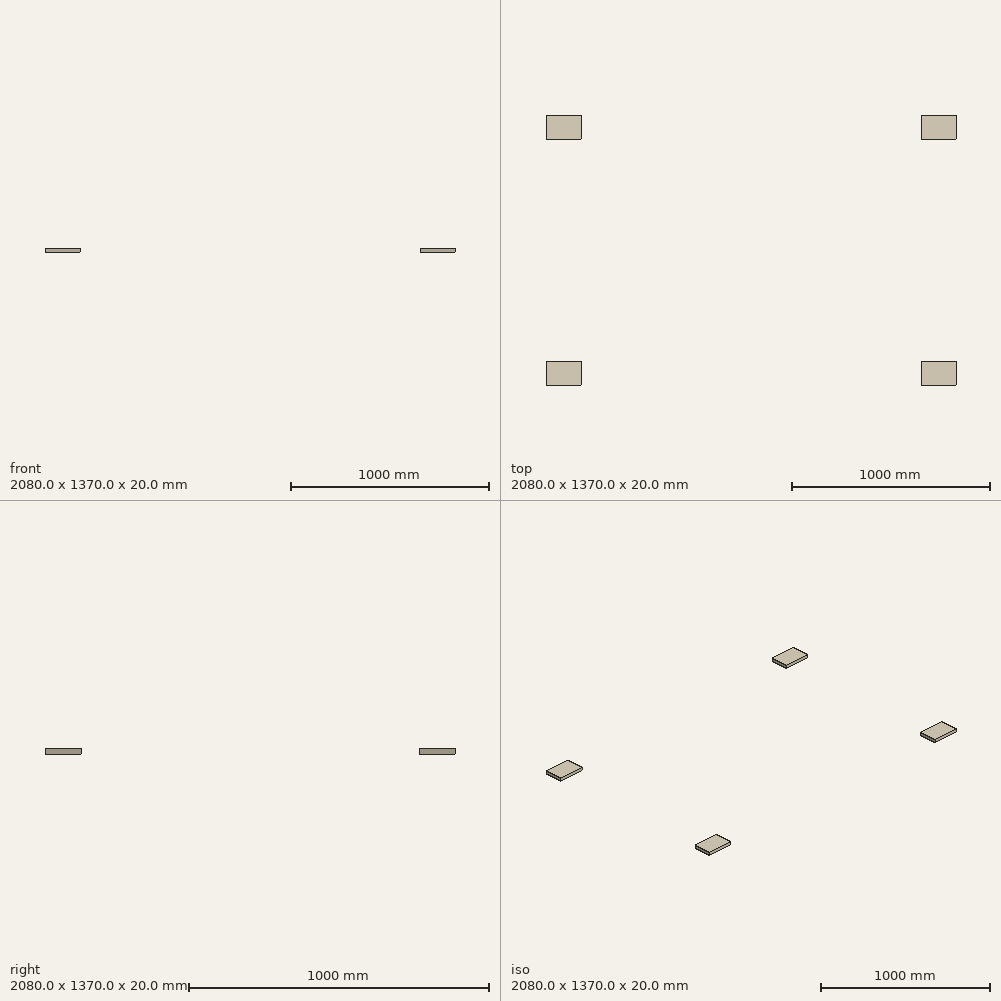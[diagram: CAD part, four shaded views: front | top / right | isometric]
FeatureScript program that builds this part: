
annotation { "Feature Type Name" : "Feature", "Feature Type Description" : "" }
export const myFeature = defineFeature(function(context is Context, id is Id, definition is map)
    precondition{}
    {
        {
            var Q0;
            Q0=qCreatedBy(makeId("Top.planeOp"),FACE);
            cPlane(context, id + "F0", {"entities" : qUnion([Q0]), "cplaneType" : CPlaneType.OFFSET, "offset" : 1000 * mm, "width" : 150 * mm, "height" : 150 * mm});
        }
        {
            var Q0;
            Q0=qCreatedBy(id+"F0.planeOp",FACE);
            var sketch = newSketch(context, id + "F1", { "sketchPlane" : qUnion([Q0])});
            skLineSegment(sketch, "E0.bottom", {"start": v(-1000, 625) * mm, "end": v(1000, 625) * mm, "construction": true});
            skLineSegment(sketch, "E0.top", {"start": v(-1000, -625) * mm, "end": v(1000, -625) * mm, "construction": true});
            skLineSegment(sketch, "E0.left", {"start": v(-1000, 625) * mm, "end": v(-1000, -625) * mm, "construction": true});
            skLineSegment(sketch, "E0.right", {"start": v(1000, 625) * mm, "end": v(1000, -625) * mm, "construction": true});
            skPoint(sketch, "E0.middle", {"position": v(0, 0) * mm});
            skLineSegment(sketch, "E1", {"start": v(-1000, 0) * mm, "end": v(1000, 0) * mm, "construction": true});
            skLineSegment(sketch, "E2", {"start": v(-350, 625) * mm, "end": v(-350, -625) * mm, "construction": true});
            skLineSegment(sketch, "E3", {"start": v(350, 625) * mm, "end": v(350, -625) * mm, "construction": true});
            skSolve(sketch);
        }
        {
            var Q0;
            Q0=qCreatedBy(makeId("Front.planeOp"),FACE);
            var Q1;
            Q1=sQuery(id+"F1.wireOp",VERTEX,"E0.top.end");
            cPlane(context, id + "F2", {"entities" : qUnion([Q0, Q1]), "cplaneType" : CPlaneType.PLANE_POINT, "offset" : 25 * mm, "width" : 150 * mm, "height" : 150 * mm});
        }
        {
            var Q0;
            Q0=qCreatedBy(id+"F2.planeOp",FACE);
            var sketch = newSketch(context, id + "F3", { "sketchPlane" : qUnion([Q0])});
            skLineSegment(sketch, "E4", {"start": v(-1000, 1000) * mm, "end": v(-1000, 0) * mm, "construction": true});
            skLineSegment(sketch, "E5", {"start": v(-1000, 650) * mm, "end": v(-650, 1000) * mm, "construction": true});
            skSolve(sketch);
        }
        {
            var Q0;
            Q0=qCreatedBy(makeId("Top.planeOp"),FACE);
            var sketch = newSketch(context, id + "F4", { "sketchPlane" : qUnion([Q0])});
            skLineSegment(sketch, "E6.bottom", {"start": v(-860, -685) * mm, "end": v(-1040, -685) * mm});
            skLineSegment(sketch, "E6.top", {"start": v(-860, -565) * mm, "end": v(-1040, -565) * mm});
            skLineSegment(sketch, "E6.left", {"start": v(-860, -685) * mm, "end": v(-860, -565) * mm});
            skLineSegment(sketch, "E6.right", {"start": v(-1040, -685) * mm, "end": v(-1040, -565) * mm});
            skPoint(sketch, "E6.middle", {"position": v(-950, -625) * mm});
            skSolve(sketch);
        }
        {
            var Q0;
            Q0=qSketchRegion(id+"F4",true);
            extrude(context, id + "F5", {"entities" : qUnion([Q0]), "depth" : 20 * mm});
        }
        {
            var Q0;
            Q0=makeQuery(id+"F5.opExtrude","SWEPT_BODY",BODY,{"disambiguationData":[OSD([sQuery(id+"F4.wireOp",EDGE,"E6.bottom"),sQuery(id+"F4.wireOp",EDGE,"E6.top"),sQuery(id+"F4.wireOp",EDGE,"E6.left"),sQuery(id+"F4.wireOp",EDGE,"E6.right")])]});
            var Q1;
            Q1=makeQuery(id+"FDKtSKcZDmq9f0q_2.splitJoint0-1.splitOp","SPLIT",BODY,{"derivedFrom":makeQuery(id+"FDKtSKcZDmq9f0q_2.splitJoint0-0.splitOp","SPLIT",BODY,{"derivedFrom":makeQuery(id+"FDKtSKcZDmq9f0q_2.sweep0.opSweep","SWEPT_BODY",BODY,{"disambiguationData":[OSD([sQuery(id+"F3.wireOp",EDGE,"E4"),sQuery(id+"FDKtSKcZDmq9f0q_2.sketch.wireOp",EDGE,"line0"),sQuery(id+"FDKtSKcZDmq9f0q_2.sketch.wireOp",EDGE,"line1"),sQuery(id+"FDKtSKcZDmq9f0q_2.sketch.wireOp",EDGE,"arc2"),sQuery(id+"FDKtSKcZDmq9f0q_2.sketch.wireOp",EDGE,"line3"),sQuery(id+"FDKtSKcZDmq9f0q_2.sketch.wireOp",EDGE,"arc4"),sQuery(id+"FDKtSKcZDmq9f0q_2.sketch.wireOp",EDGE,"line5"),sQuery(id+"FDKtSKcZDmq9f0q_2.sketch.wireOp",EDGE,"arc6"),sQuery(id+"FDKtSKcZDmq9f0q_2.sketch.wireOp",EDGE,"line7"),sQuery(id+"FDKtSKcZDmq9f0q_2.sketch.wireOp",EDGE,"arc8"),sQuery(id+"FDKtSKcZDmq9f0q_2.sketch.wireOp",EDGE,"line9"),sQuery(id+"FDKtSKcZDmq9f0q_2.sketch.wireOp",EDGE,"line10"),sQuery(id+"FDKtSKcZDmq9f0q_2.sketch.wireOp",EDGE,"line11"),sQuery(id+"FDKtSKcZDmq9f0q_2.sketch.wireOp",EDGE,"arc12"),sQuery(id+"FDKtSKcZDmq9f0q_2.sketch.wireOp",EDGE,"line13"),sQuery(id+"FDKtSKcZDmq9f0q_2.sketch.wireOp",EDGE,"arc14"),sQuery(id+"FDKtSKcZDmq9f0q_2.sketch.wireOp",EDGE,"line15"),sQuery(id+"FDKtSKcZDmq9f0q_2.sketch.wireOp",EDGE,"arc16"),sQuery(id+"FDKtSKcZDmq9f0q_2.sketch.wireOp",EDGE,"line17"),sQuery(id+"FDKtSKcZDmq9f0q_2.sketch.wireOp",EDGE,"arc18"),sQuery(id+"FDKtSKcZDmq9f0q_2.sketch.wireOp",EDGE,"line19")])]})})});
            var Q2;
            Q2=makeQuery(id+"FrrdRgtmGFbWE7B_3.splitJoint0-1.splitOp","SPLIT",BODY,{"derivedFrom":makeQuery(id+"FrrdRgtmGFbWE7B_3.splitJoint0-0.splitOp","SPLIT",BODY,{"derivedFrom":makeQuery(id+"FrrdRgtmGFbWE7B_3.sweep0.opSweep","SWEPT_BODY",BODY,{"disambiguationData":[OSD([sQuery(id+"F3.wireOp",EDGE,"E5"),sQuery(id+"FrrdRgtmGFbWE7B_3.sketch.wireOp",EDGE,"line0"),sQuery(id+"FrrdRgtmGFbWE7B_3.sketch.wireOp",EDGE,"line1"),sQuery(id+"FrrdRgtmGFbWE7B_3.sketch.wireOp",EDGE,"arc2"),sQuery(id+"FrrdRgtmGFbWE7B_3.sketch.wireOp",EDGE,"line3"),sQuery(id+"FrrdRgtmGFbWE7B_3.sketch.wireOp",EDGE,"arc4"),sQuery(id+"FrrdRgtmGFbWE7B_3.sketch.wireOp",EDGE,"line5"),sQuery(id+"FrrdRgtmGFbWE7B_3.sketch.wireOp",EDGE,"arc6"),sQuery(id+"FrrdRgtmGFbWE7B_3.sketch.wireOp",EDGE,"line7"),sQuery(id+"FrrdRgtmGFbWE7B_3.sketch.wireOp",EDGE,"arc8"),sQuery(id+"FrrdRgtmGFbWE7B_3.sketch.wireOp",EDGE,"line9"),sQuery(id+"FrrdRgtmGFbWE7B_3.sketch.wireOp",EDGE,"line10"),sQuery(id+"FrrdRgtmGFbWE7B_3.sketch.wireOp",EDGE,"line11"),sQuery(id+"FrrdRgtmGFbWE7B_3.sketch.wireOp",EDGE,"arc12"),sQuery(id+"FrrdRgtmGFbWE7B_3.sketch.wireOp",EDGE,"line13"),sQuery(id+"FrrdRgtmGFbWE7B_3.sketch.wireOp",EDGE,"arc14"),sQuery(id+"FrrdRgtmGFbWE7B_3.sketch.wireOp",EDGE,"line15"),sQuery(id+"FrrdRgtmGFbWE7B_3.sketch.wireOp",EDGE,"arc16"),sQuery(id+"FrrdRgtmGFbWE7B_3.sketch.wireOp",EDGE,"line17"),sQuery(id+"FrrdRgtmGFbWE7B_3.sketch.wireOp",EDGE,"arc18"),sQuery(id+"FrrdRgtmGFbWE7B_3.sketch.wireOp",EDGE,"line19")])]})})});
            var Q3;
            Q3=qCreatedBy(makeId("Right.planeOp"),FACE);
            mirror(context, id + "F6", {"entities" : qUnion([Q0, Q1, Q2]), "mirrorPlane" : qUnion([Q3])});
        }
        {
            var Q0;
            Q0=makeQuery(id+"F5.opExtrude","SWEPT_BODY",BODY,{"disambiguationData":[OSD([sQuery(id+"F4.wireOp",EDGE,"E6.bottom"),sQuery(id+"F4.wireOp",EDGE,"E6.top"),sQuery(id+"F4.wireOp",EDGE,"E6.left"),sQuery(id+"F4.wireOp",EDGE,"E6.right")])]});
            var Q1;
            Q1=makeQuery(id+"F6.opPattern","COPY",BODY,{"derivedFrom":makeQuery(id+"F5.opExtrude","SWEPT_BODY",BODY,{"disambiguationData":[OSD([sQuery(id+"F4.wireOp",EDGE,"E6.bottom"),sQuery(id+"F4.wireOp",EDGE,"E6.top"),sQuery(id+"F4.wireOp",EDGE,"E6.left"),sQuery(id+"F4.wireOp",EDGE,"E6.right")])]}),"instanceName":"1"});
            var Q2;
            Q2=makeQuery(id+"F6.opPattern","COPY",BODY,{"derivedFrom":makeQuery(id+"FrrdRgtmGFbWE7B_3.splitJoint0-1.splitOp","SPLIT",BODY,{"derivedFrom":makeQuery(id+"FrrdRgtmGFbWE7B_3.splitJoint0-0.splitOp","SPLIT",BODY,{"derivedFrom":makeQuery(id+"FrrdRgtmGFbWE7B_3.sweep0.opSweep","SWEPT_BODY",BODY,{"disambiguationData":[OSD([sQuery(id+"F3.wireOp",EDGE,"E5"),sQuery(id+"FrrdRgtmGFbWE7B_3.sketch.wireOp",EDGE,"line0"),sQuery(id+"FrrdRgtmGFbWE7B_3.sketch.wireOp",EDGE,"line1"),sQuery(id+"FrrdRgtmGFbWE7B_3.sketch.wireOp",EDGE,"arc2"),sQuery(id+"FrrdRgtmGFbWE7B_3.sketch.wireOp",EDGE,"line3"),sQuery(id+"FrrdRgtmGFbWE7B_3.sketch.wireOp",EDGE,"arc4"),sQuery(id+"FrrdRgtmGFbWE7B_3.sketch.wireOp",EDGE,"line5"),sQuery(id+"FrrdRgtmGFbWE7B_3.sketch.wireOp",EDGE,"arc6"),sQuery(id+"FrrdRgtmGFbWE7B_3.sketch.wireOp",EDGE,"line7"),sQuery(id+"FrrdRgtmGFbWE7B_3.sketch.wireOp",EDGE,"arc8"),sQuery(id+"FrrdRgtmGFbWE7B_3.sketch.wireOp",EDGE,"line9"),sQuery(id+"FrrdRgtmGFbWE7B_3.sketch.wireOp",EDGE,"line10"),sQuery(id+"FrrdRgtmGFbWE7B_3.sketch.wireOp",EDGE,"line11"),sQuery(id+"FrrdRgtmGFbWE7B_3.sketch.wireOp",EDGE,"arc12"),sQuery(id+"FrrdRgtmGFbWE7B_3.sketch.wireOp",EDGE,"line13"),sQuery(id+"FrrdRgtmGFbWE7B_3.sketch.wireOp",EDGE,"arc14"),sQuery(id+"FrrdRgtmGFbWE7B_3.sketch.wireOp",EDGE,"line15"),sQuery(id+"FrrdRgtmGFbWE7B_3.sketch.wireOp",EDGE,"arc16"),sQuery(id+"FrrdRgtmGFbWE7B_3.sketch.wireOp",EDGE,"line17"),sQuery(id+"FrrdRgtmGFbWE7B_3.sketch.wireOp",EDGE,"arc18"),sQuery(id+"FrrdRgtmGFbWE7B_3.sketch.wireOp",EDGE,"line19")])]})})}),"instanceName":"1"});
            var Q3;
            Q3=makeQuery(id+"FDKtSKcZDmq9f0q_2.splitJoint0-1.splitOp","SPLIT",BODY,{"derivedFrom":makeQuery(id+"FDKtSKcZDmq9f0q_2.splitJoint0-0.splitOp","SPLIT",BODY,{"derivedFrom":makeQuery(id+"FDKtSKcZDmq9f0q_2.sweep0.opSweep","SWEPT_BODY",BODY,{"disambiguationData":[OSD([sQuery(id+"F3.wireOp",EDGE,"E4"),sQuery(id+"FDKtSKcZDmq9f0q_2.sketch.wireOp",EDGE,"line0"),sQuery(id+"FDKtSKcZDmq9f0q_2.sketch.wireOp",EDGE,"line1"),sQuery(id+"FDKtSKcZDmq9f0q_2.sketch.wireOp",EDGE,"arc2"),sQuery(id+"FDKtSKcZDmq9f0q_2.sketch.wireOp",EDGE,"line3"),sQuery(id+"FDKtSKcZDmq9f0q_2.sketch.wireOp",EDGE,"arc4"),sQuery(id+"FDKtSKcZDmq9f0q_2.sketch.wireOp",EDGE,"line5"),sQuery(id+"FDKtSKcZDmq9f0q_2.sketch.wireOp",EDGE,"arc6"),sQuery(id+"FDKtSKcZDmq9f0q_2.sketch.wireOp",EDGE,"line7"),sQuery(id+"FDKtSKcZDmq9f0q_2.sketch.wireOp",EDGE,"arc8"),sQuery(id+"FDKtSKcZDmq9f0q_2.sketch.wireOp",EDGE,"line9"),sQuery(id+"FDKtSKcZDmq9f0q_2.sketch.wireOp",EDGE,"line10"),sQuery(id+"FDKtSKcZDmq9f0q_2.sketch.wireOp",EDGE,"line11"),sQuery(id+"FDKtSKcZDmq9f0q_2.sketch.wireOp",EDGE,"arc12"),sQuery(id+"FDKtSKcZDmq9f0q_2.sketch.wireOp",EDGE,"line13"),sQuery(id+"FDKtSKcZDmq9f0q_2.sketch.wireOp",EDGE,"arc14"),sQuery(id+"FDKtSKcZDmq9f0q_2.sketch.wireOp",EDGE,"line15"),sQuery(id+"FDKtSKcZDmq9f0q_2.sketch.wireOp",EDGE,"arc16"),sQuery(id+"FDKtSKcZDmq9f0q_2.sketch.wireOp",EDGE,"line17"),sQuery(id+"FDKtSKcZDmq9f0q_2.sketch.wireOp",EDGE,"arc18"),sQuery(id+"FDKtSKcZDmq9f0q_2.sketch.wireOp",EDGE,"line19")])]})})});
            var Q4;
            Q4=makeQuery(id+"F6.opPattern","COPY",BODY,{"derivedFrom":makeQuery(id+"FDKtSKcZDmq9f0q_2.splitJoint0-1.splitOp","SPLIT",BODY,{"derivedFrom":makeQuery(id+"FDKtSKcZDmq9f0q_2.splitJoint0-0.splitOp","SPLIT",BODY,{"derivedFrom":makeQuery(id+"FDKtSKcZDmq9f0q_2.sweep0.opSweep","SWEPT_BODY",BODY,{"disambiguationData":[OSD([sQuery(id+"F3.wireOp",EDGE,"E4"),sQuery(id+"FDKtSKcZDmq9f0q_2.sketch.wireOp",EDGE,"line0"),sQuery(id+"FDKtSKcZDmq9f0q_2.sketch.wireOp",EDGE,"line1"),sQuery(id+"FDKtSKcZDmq9f0q_2.sketch.wireOp",EDGE,"arc2"),sQuery(id+"FDKtSKcZDmq9f0q_2.sketch.wireOp",EDGE,"line3"),sQuery(id+"FDKtSKcZDmq9f0q_2.sketch.wireOp",EDGE,"arc4"),sQuery(id+"FDKtSKcZDmq9f0q_2.sketch.wireOp",EDGE,"line5"),sQuery(id+"FDKtSKcZDmq9f0q_2.sketch.wireOp",EDGE,"arc6"),sQuery(id+"FDKtSKcZDmq9f0q_2.sketch.wireOp",EDGE,"line7"),sQuery(id+"FDKtSKcZDmq9f0q_2.sketch.wireOp",EDGE,"arc8"),sQuery(id+"FDKtSKcZDmq9f0q_2.sketch.wireOp",EDGE,"line9"),sQuery(id+"FDKtSKcZDmq9f0q_2.sketch.wireOp",EDGE,"line10"),sQuery(id+"FDKtSKcZDmq9f0q_2.sketch.wireOp",EDGE,"line11"),sQuery(id+"FDKtSKcZDmq9f0q_2.sketch.wireOp",EDGE,"arc12"),sQuery(id+"FDKtSKcZDmq9f0q_2.sketch.wireOp",EDGE,"line13"),sQuery(id+"FDKtSKcZDmq9f0q_2.sketch.wireOp",EDGE,"arc14"),sQuery(id+"FDKtSKcZDmq9f0q_2.sketch.wireOp",EDGE,"line15"),sQuery(id+"FDKtSKcZDmq9f0q_2.sketch.wireOp",EDGE,"arc16"),sQuery(id+"FDKtSKcZDmq9f0q_2.sketch.wireOp",EDGE,"line17"),sQuery(id+"FDKtSKcZDmq9f0q_2.sketch.wireOp",EDGE,"arc18"),sQuery(id+"FDKtSKcZDmq9f0q_2.sketch.wireOp",EDGE,"line19")])]})})}),"instanceName":"1"});
            var Q5;
            Q5=makeQuery(id+"FrrdRgtmGFbWE7B_3.splitJoint0-1.splitOp","SPLIT",BODY,{"derivedFrom":makeQuery(id+"FrrdRgtmGFbWE7B_3.splitJoint0-0.splitOp","SPLIT",BODY,{"derivedFrom":makeQuery(id+"FrrdRgtmGFbWE7B_3.sweep0.opSweep","SWEPT_BODY",BODY,{"disambiguationData":[OSD([sQuery(id+"F3.wireOp",EDGE,"E5"),sQuery(id+"FrrdRgtmGFbWE7B_3.sketch.wireOp",EDGE,"line0"),sQuery(id+"FrrdRgtmGFbWE7B_3.sketch.wireOp",EDGE,"line1"),sQuery(id+"FrrdRgtmGFbWE7B_3.sketch.wireOp",EDGE,"arc2"),sQuery(id+"FrrdRgtmGFbWE7B_3.sketch.wireOp",EDGE,"line3"),sQuery(id+"FrrdRgtmGFbWE7B_3.sketch.wireOp",EDGE,"arc4"),sQuery(id+"FrrdRgtmGFbWE7B_3.sketch.wireOp",EDGE,"line5"),sQuery(id+"FrrdRgtmGFbWE7B_3.sketch.wireOp",EDGE,"arc6"),sQuery(id+"FrrdRgtmGFbWE7B_3.sketch.wireOp",EDGE,"line7"),sQuery(id+"FrrdRgtmGFbWE7B_3.sketch.wireOp",EDGE,"arc8"),sQuery(id+"FrrdRgtmGFbWE7B_3.sketch.wireOp",EDGE,"line9"),sQuery(id+"FrrdRgtmGFbWE7B_3.sketch.wireOp",EDGE,"line10"),sQuery(id+"FrrdRgtmGFbWE7B_3.sketch.wireOp",EDGE,"line11"),sQuery(id+"FrrdRgtmGFbWE7B_3.sketch.wireOp",EDGE,"arc12"),sQuery(id+"FrrdRgtmGFbWE7B_3.sketch.wireOp",EDGE,"line13"),sQuery(id+"FrrdRgtmGFbWE7B_3.sketch.wireOp",EDGE,"arc14"),sQuery(id+"FrrdRgtmGFbWE7B_3.sketch.wireOp",EDGE,"line15"),sQuery(id+"FrrdRgtmGFbWE7B_3.sketch.wireOp",EDGE,"arc16"),sQuery(id+"FrrdRgtmGFbWE7B_3.sketch.wireOp",EDGE,"line17"),sQuery(id+"FrrdRgtmGFbWE7B_3.sketch.wireOp",EDGE,"arc18"),sQuery(id+"FrrdRgtmGFbWE7B_3.sketch.wireOp",EDGE,"line19")])]})})});
            var Q6;
            Q6=qCreatedBy(makeId("Front.planeOp"),FACE);
            mirror(context, id + "F7", {"entities" : qUnion([Q0, Q1, Q2, Q3, Q4, Q5]), "mirrorPlane" : qUnion([Q6])});
        }
    });
